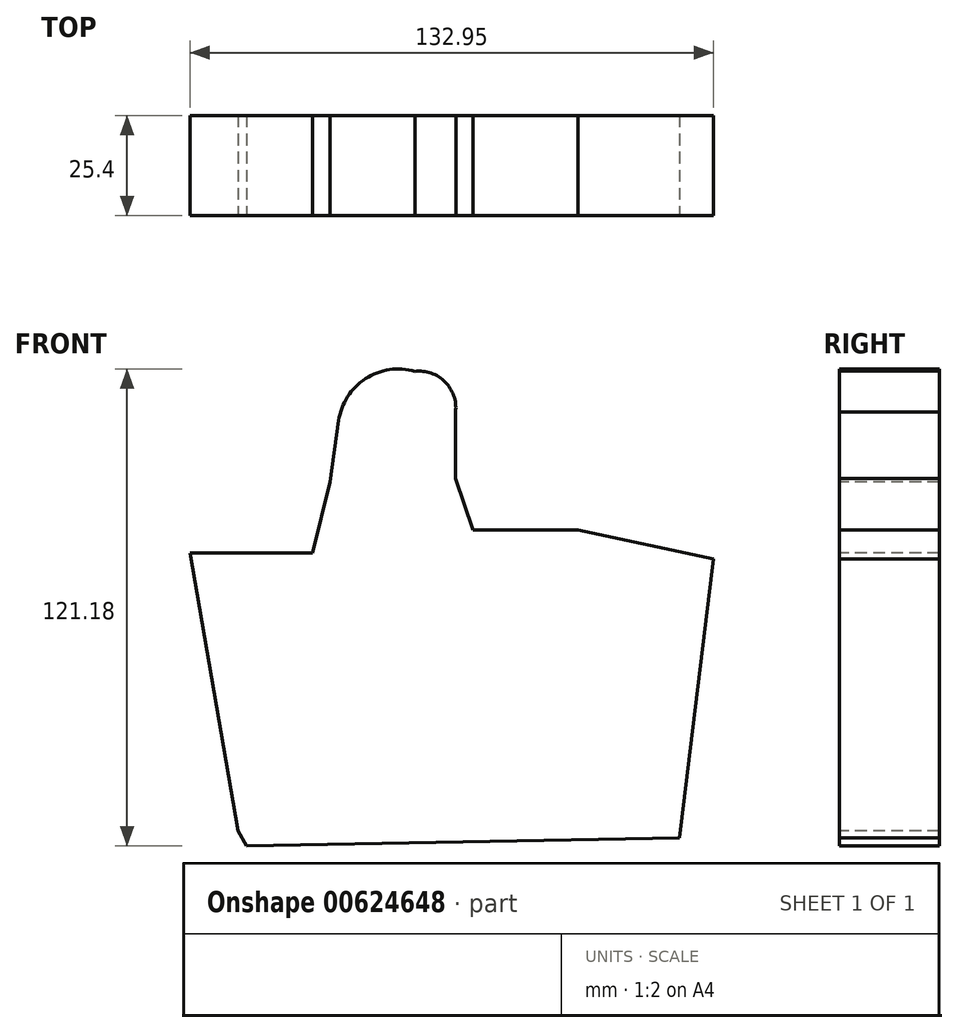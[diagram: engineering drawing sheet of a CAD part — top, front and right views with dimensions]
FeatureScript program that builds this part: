
annotation { "Feature Type Name" : "Feature", "Feature Type Description" : "" }
export const myFeature = defineFeature(function(context is Context, id is Id, definition is map)
    precondition{}
    {
        {
            var Q0;
            Q0=qCreatedBy(makeId("Front.planeOp"),FACE);
            var sketch = newSketch(context, id + "F0", { "sketchPlane" : qUnion([Q0])});
            skLineSegment(sketch, "E0", {"start": v(-65.43, 0) * mm, "end": v(-34.33, 0) * mm});
            skLineSegment(sketch, "E1", {"start": v(-34.33, 0) * mm, "end": v(-29.84, 18.12) * mm});
            skLineSegment(sketch, "E2", {"start": v(-29.84, 18.12) * mm, "end": v(-27.68, 33.63) * mm});
            skArc(sketch, "E3", {"start": v(-8.31, 46.17) * mm, "mid": v(-20.86, 44.32) * mm, "end": v(-27.68, 33.63) * mm});
            skArc(sketch, "E4", {"start": v(2.01, 35.87) * mm, "mid": v(-0.66, 43.51) * mm, "end": v(-8.31, 46.17) * mm});
            skLineSegment(sketch, "E5", {"start": v(2.01, 35.87) * mm, "end": v(2.01, 18.93) * mm});
            skLineSegment(sketch, "E6", {"start": v(2.01, 18.93) * mm, "end": v(6.41, 5.88) * mm});
            skLineSegment(sketch, "E7", {"start": v(6.41, 5.88) * mm, "end": v(33.15, 5.88) * mm});
            skLineSegment(sketch, "E8", {"start": v(33.15, 5.88) * mm, "end": v(67.52, -1.52) * mm});
            skLineSegment(sketch, "E9", {"start": v(67.52, -1.52) * mm, "end": v(58.94, -72.35) * mm});
            skLineSegment(sketch, "E10", {"start": v(58.94, -72.35) * mm, "end": v(-51.04, -74.4) * mm});
            skLineSegment(sketch, "E11", {"start": v(-51.04, -74.4) * mm, "end": v(-53.19, -70.55) * mm});
            skLineSegment(sketch, "E12", {"start": v(-53.19, -70.55) * mm, "end": v(-65.43, 0) * mm});
            skSolve(sketch);
        }
        {
            var Q0;
            Q0 = qConstructionFilter(qBodyType(qCreatedBy(id + "F0" ,EDGE), BodyType.WIRE), ConstructionObject.NO);
            extrude(context, id + "F1", {"bodyType" : ToolBodyType.SURFACE, "surfaceEntities" : qUnion([Q0]), "depth" : 25.4 * mm, "offsetDistance" : 25.4 * mm});
        }
    });
